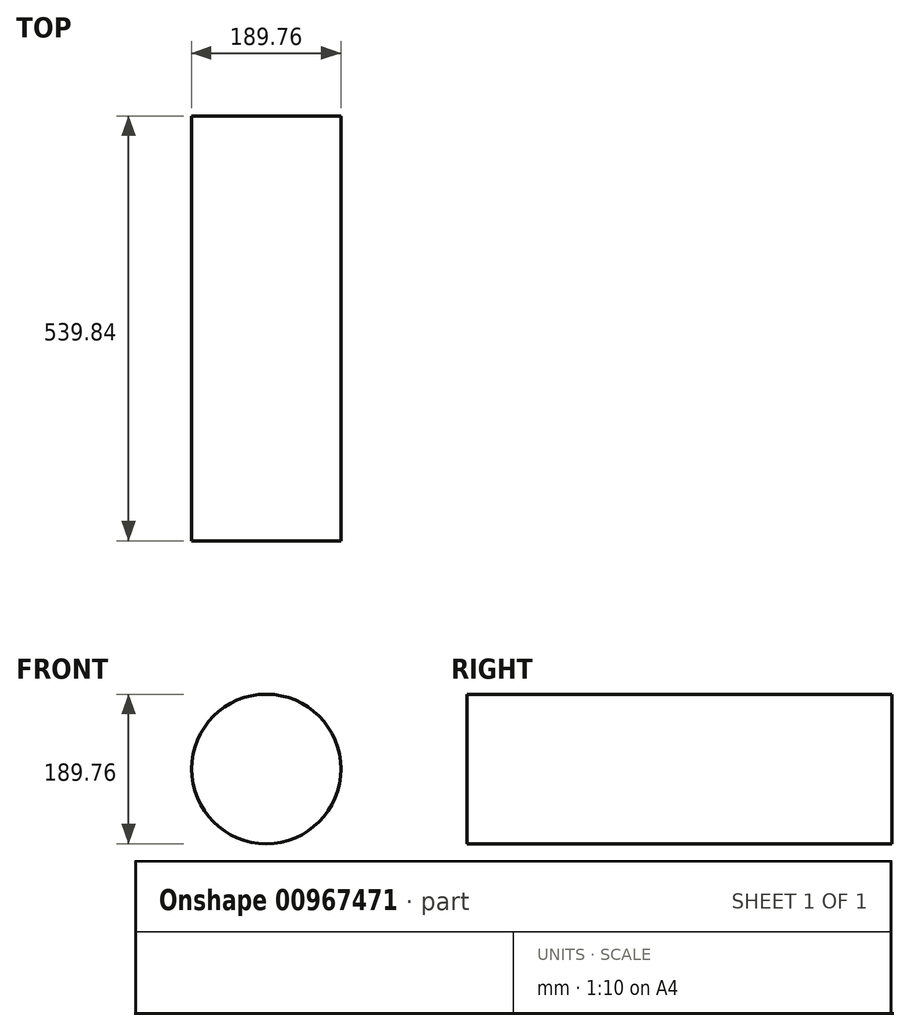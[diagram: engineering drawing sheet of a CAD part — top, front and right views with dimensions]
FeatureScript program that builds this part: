
annotation { "Feature Type Name" : "Feature", "Feature Type Description" : "" }
export const myFeature = defineFeature(function(context is Context, id is Id, definition is map)
    precondition{}
    {
        {
            var Q0;
            Q0=qCreatedBy(makeId("Front.planeOp"),FACE);
            var sketch = newSketch(context, id + "F0", { "sketchPlane" : qUnion([Q0])});
            skCircle(sketch, "E0", {"center": v(0, 0) * mm, "radius": 94.88 * mm});
            skSolve(sketch);
        }
        {
            var Q0;
            Q0=makeQuery(id+"F0.imprint","IMPRINT",FACE,{"disambiguationData":[TD([[makeQuery(id+"F0.imprint","IMPRINT",EDGE,{"derivedFrom":sQuery(id+"F0.wireOp",EDGE,"E0")}),1.0]])]});
            extrude(context, id + "F1", {"entities" : qUnion([Q0]), "depth" : 539.84 * mm, "offsetDistance" : 25.4 * mm});
        }
    });
